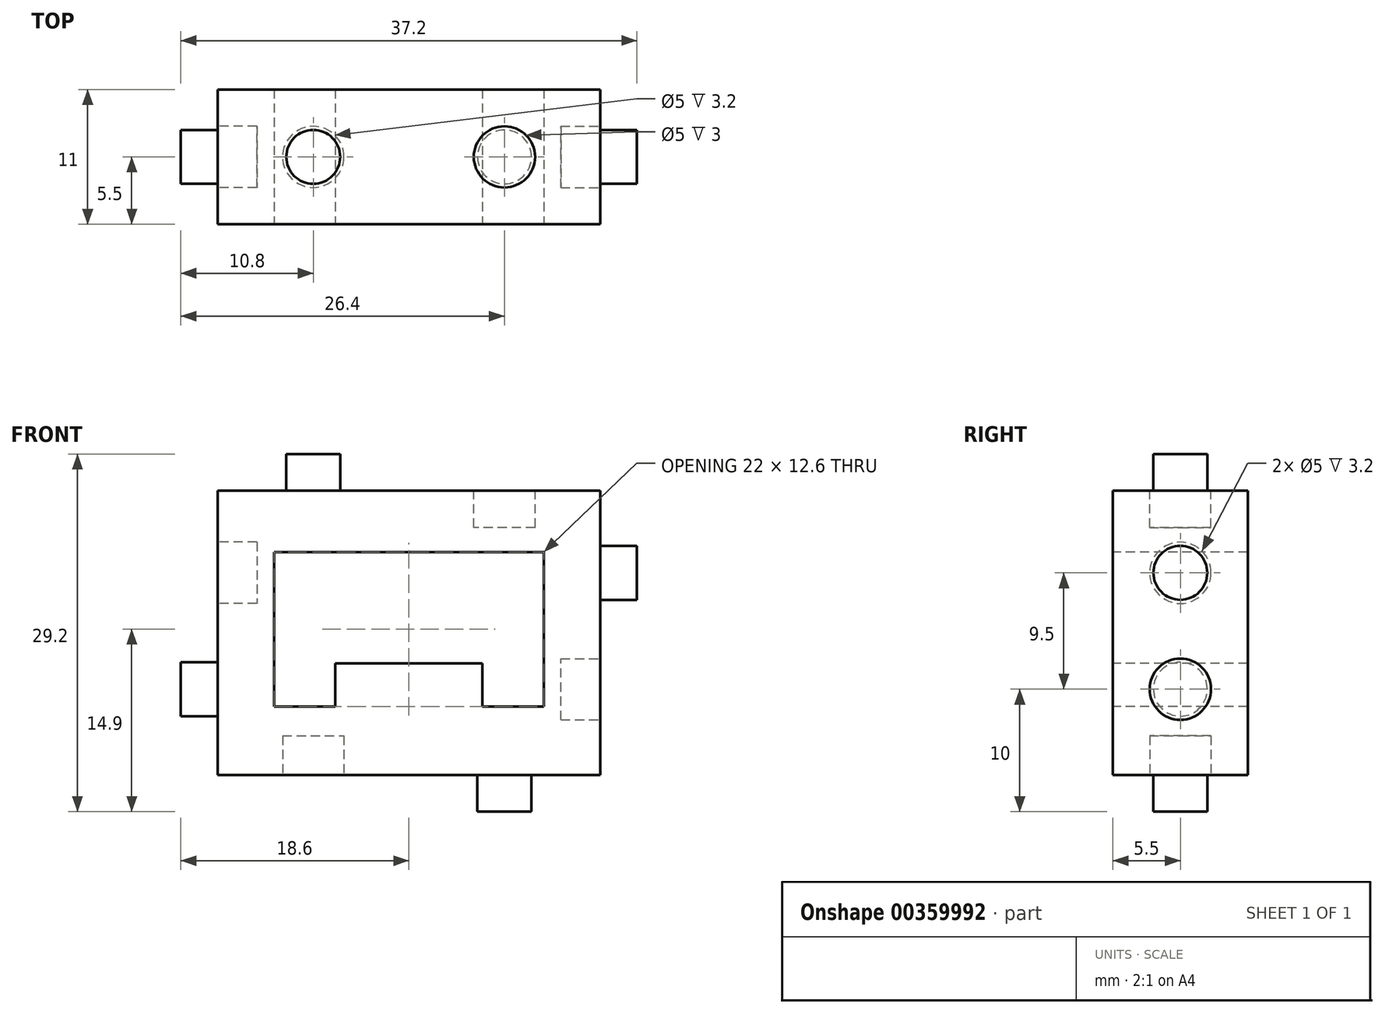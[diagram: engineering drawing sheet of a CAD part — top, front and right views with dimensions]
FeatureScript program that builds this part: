
annotation { "Feature Type Name" : "Feature", "Feature Type Description" : "" }
export const myFeature = defineFeature(function(context is Context, id is Id, definition is map)
    precondition{}
    {
        {
            var Q0;
            Q0=qCreatedBy(makeId("Top.planeOp"),FACE);
            var sketch = newSketch(context, id + "F0", { "sketchPlane" : qUnion([Q0])});
            skLineSegment(sketch, "E0.bottom", {"start": v(-15.6, 5.5) * mm, "end": v(15.6, 5.5) * mm});
            skLineSegment(sketch, "E0.top", {"start": v(-15.6, -5.5) * mm, "end": v(15.6, -5.5) * mm});
            skLineSegment(sketch, "E0.left", {"start": v(-15.6, 5.5) * mm, "end": v(-15.6, -5.5) * mm});
            skLineSegment(sketch, "E0.right", {"start": v(15.6, 5.5) * mm, "end": v(15.6, -5.5) * mm});
            skLineSegment(sketch, "E1", {"start": v(-7.8, 0) * mm, "end": v(-7.8, 14.25) * mm, "construction": true});
            skLineSegment(sketch, "E2", {"start": v(0, 13.9) * mm, "end": v(0, -15.19) * mm});
            skSolve(sketch);
        }
        {
            var Q0;
            Q0=makeQuery(id+"F0.imprint","IMPRINT",FACE,{"disambiguationData":[TD([[makeQuery(id+"F0.imprint","IMPRINT",EDGE,{"derivedFrom":sQuery(id+"F0.wireOp",EDGE,"E0.bottom")}),-1.0]])]});
            extrude(context, id + "F1", {"entities" : qUnion([Q0]), "depth" : 23.2 * mm});
        }
        {
            var Q0;
            Q0=makeQuery(id+"F1.opExtrude","SWEPT_FACE",FACE,{"disambiguationData":[OSD([sQuery(id+"F0.wireOp",EDGE,"E0.top")])]});
            var sketch = newSketch(context, id + "F2", { "sketchPlane" : qUnion([Q0])});
            skLineSegment(sketch, "E3.MirrorCS", {"start": v(-11, 18.2) * mm, "end": v(-11, 5.6) * mm});
            skLineSegment(sketch, "E4.MirrorCS", {"start": v(-6, 5.6) * mm, "end": v(-6, 9.1) * mm});
            skPoint(sketch, "E5.MirrorP", {"position": v(-11, 5.6) * mm});
            skLineSegment(sketch, "E6.MirrorCS", {"start": v(-11, 5.6) * mm, "end": v(-6, 5.6) * mm});
            skLineSegment(sketch, "E7.MirrorCS", {"start": v(0, 9.1) * mm, "end": v(-6, 9.1) * mm});
            skLineSegment(sketch, "E8.MirrorCS", {"start": v(0, 18.2) * mm, "end": v(-11, 18.2) * mm});
            skLineSegment(sketch, "E9.MirrorCS", {"start": v(0, 18.2) * mm, "end": v(11, 18.2) * mm});
            skLineSegment(sketch, "E10.MirrorCS", {"start": v(11, 18.2) * mm, "end": v(11, 5.6) * mm});
            skLineSegment(sketch, "E11.MirrorCS", {"start": v(11, 5.6) * mm, "end": v(6, 5.6) * mm});
            skLineSegment(sketch, "E12.MirrorCS", {"start": v(6, 5.6) * mm, "end": v(6, 9.1) * mm});
            skLineSegment(sketch, "E13.MirrorCS", {"start": v(0, 9.1) * mm, "end": v(6, 9.1) * mm});
            skSolve(sketch);
        }
        {
            var Q0;
            Q0=makeQuery(id+"F2.imprint","IMPRINT",FACE,{"disambiguationData":[TD([[makeQuery(id+"F2.imprint","IMPRINT",EDGE,{"derivedFrom":sQuery(id+"F2.wireOp",EDGE,"jR3wVv9S-Wn4a-DM1W-meKF-9iTBe72kzQsL.bottom")}),-1.0]])]});
            var Q1;
            Q1=makeQuery(id+"F2.imprint","IMPRINT",FACE,{"disambiguationData":[TD([[makeQuery(id+"F2.imprint","IMPRINT",EDGE,{"derivedFrom":sQuery(id+"F2.wireOp",EDGE,"E3.MirrorCS")}),1.0]])]});
            extrude(context, id + "F3", {"entities" : qUnion([Q0, Q1]), "operationType" : NewBodyOperationType.REMOVE, "oppositeDirection" : true, "depth" : 25 * mm});
        }
        {
            var Q0;
            Q0=makeQuery(id+"F1.opExtrude","CAP_FACE",FACE,{"disambiguationData":[OSD([sQuery(id+"F0.wireOp",EDGE,"E0.bottom"),sQuery(id+"F0.wireOp",EDGE,"E0.top"),sQuery(id+"F0.wireOp",EDGE,"E0.left"),sQuery(id+"F0.wireOp",EDGE,"E0.right")])],"isStart":true});
            var sketch = newSketch(context, id + "F4", { "sketchPlane" : qUnion([Q0])});
            skCircle(sketch, "E14", {"center": v(-7.8, 0) * mm, "radius": 2.5 * mm});
            skSolve(sketch);
        }
        {
            var Q0;
            Q0 = qSketchRegion(id + "F4", true);
            extrude(context, id + "F5", {"entities" : qUnion([Q0]), "operationType" : NewBodyOperationType.REMOVE, "oppositeDirection" : true, "depth" : 3.2 * mm});
        }
        {
            var Q0;
            Q0=makeQuery(id+"F1.opExtrude","CAP_FACE",FACE,{"disambiguationData":[OSD([sQuery(id+"F0.wireOp",EDGE,"E0.bottom"),sQuery(id+"F0.wireOp",EDGE,"E0.top"),sQuery(id+"F0.wireOp",EDGE,"E0.left"),sQuery(id+"F0.wireOp",EDGE,"E0.right")])],"isStart":true});
            var sketch = newSketch(context, id + "F6", { "sketchPlane" : qUnion([Q0])});
            skCircle(sketch, "E15.0", {"center": v(-7.8, 0) * mm, "radius": 2.2 * mm, "construction": true});
            skCircle(sketch, "E16.MirrorC", {"center": v(7.8, 0) * mm, "radius": 2.2 * mm});
            skSolve(sketch);
        }
        {
            var Q0;
            Q0 = qSketchRegion(id + "F6", true);
            extrude(context, id + "F7", {"entities" : qUnion([Q0]), "operationType" : NewBodyOperationType.ADD, "depth" : 3 * mm});
        }
        {
            var Q0;
            Q0=makeQuery(id+"F1.opExtrude","CAP_FACE",FACE,{"disambiguationData":[OSD([sQuery(id+"F0.wireOp",EDGE,"E0.bottom"),sQuery(id+"F0.wireOp",EDGE,"E0.top"),sQuery(id+"F0.wireOp",EDGE,"E0.left"),sQuery(id+"F0.wireOp",EDGE,"E0.right")])],"isStart":false});
            var sketch = newSketch(context, id + "F8", { "sketchPlane" : qUnion([Q0])});
            skCircle(sketch, "E17", {"center": v(-7.8, 0) * mm, "radius": 2.2 * mm});
            skSolve(sketch);
        }
        {
            var Q0;
            Q0 = qSketchRegion(id + "F8", true);
            extrude(context, id + "F9", {"entities" : qUnion([Q0]), "operationType" : NewBodyOperationType.ADD, "depth" : 3 * mm});
        }
        {
            var Q0;
            Q0=makeQuery(id+"F1.opExtrude","CAP_FACE",FACE,{"disambiguationData":[OSD([sQuery(id+"F0.wireOp",EDGE,"E0.bottom"),sQuery(id+"F0.wireOp",EDGE,"E0.top"),sQuery(id+"F0.wireOp",EDGE,"E0.left"),sQuery(id+"F0.wireOp",EDGE,"E0.right")])],"isStart":false});
            var sketch = newSketch(context, id + "F10", { "sketchPlane" : qUnion([Q0])});
            skCircle(sketch, "E18", {"center": v(7.8, 0) * mm, "radius": 2.5 * mm});
            skSolve(sketch);
        }
        {
            var Q0;
            Q0=makeQuery(id+"F10.imprint","IMPRINT",FACE,{"disambiguationData":[TD([[makeQuery(id+"F10.imprint","IMPRINT",EDGE,{"derivedFrom":sQuery(id+"F10.wireOp",EDGE,"E18")}),1.0]])]});
            var Q1;
            Q1=sQuery(id+"F10.wireOp",EDGE,"E18");
            extrude(context, id + "F11", {"entities" : qUnion([Q0]), "operationType" : NewBodyOperationType.REMOVE, "surfaceEntities" : qUnion([Q1]), "oppositeDirection" : true, "depth" : 3 * mm});
        }
        {
            var Q0;
            Q0=makeQuery(id+"F1.opExtrude","SWEPT_FACE",FACE,{"disambiguationData":[OSD([sQuery(id+"F0.wireOp",EDGE,"E0.right")])]});
            var sketch = newSketch(context, id + "F12", { "sketchPlane" : qUnion([Q0])});
            skCircle(sketch, "E19", {"center": v(0, 7) * mm, "radius": 2.5 * mm});
            skSolve(sketch);
        }
        {
            var Q0;
            Q0=makeQuery(id+"F12.imprint","IMPRINT",FACE,{"disambiguationData":[TD([[makeQuery(id+"F12.imprint","IMPRINT",EDGE,{"derivedFrom":sQuery(id+"F12.wireOp",EDGE,"E19")}),-1.0]])]});
            var sketch = newSketch(context, id + "F13", { "sketchPlane" : qUnion([Q0])});
            skCircle(sketch, "E20", {"center": v(0, 16.5) * mm, "radius": 2.2 * mm});
            skSolve(sketch);
        }
        {
            var Q0;
            Q0=makeQuery(id+"F13.imprint","IMPRINT",FACE,{"disambiguationData":[TD([[makeQuery(id+"F13.imprint","IMPRINT",EDGE,{"derivedFrom":sQuery(id+"F13.wireOp",EDGE,"E20")}),1.0]])]});
            var Q1;
            Q1=sQuery(id+"F13.wireOp",EDGE,"E20");
            extrude(context, id + "F14", {"entities" : qUnion([Q0]), "operationType" : NewBodyOperationType.ADD, "surfaceEntities" : qUnion([Q1]), "depth" : 3 * mm});
        }
        {
            var Q0;
            Q0=makeQuery(id+"F12.imprint","IMPRINT",FACE,{"disambiguationData":[TD([[makeQuery(id+"F12.imprint","IMPRINT",EDGE,{"derivedFrom":sQuery(id+"F12.wireOp",EDGE,"E19")}),1.0]])]});
            var Q1;
            Q1=sQuery(id+"F12.wireOp",EDGE,"E19");
            extrude(context, id + "F15", {"entities" : qUnion([Q0]), "operationType" : NewBodyOperationType.REMOVE, "surfaceEntities" : qUnion([Q1]), "oppositeDirection" : true, "depth" : 3.2 * mm});
        }
        {
            var Q0;
            Q0=makeQuery(id+"F1.opExtrude","SWEPT_FACE",FACE,{"disambiguationData":[OSD([sQuery(id+"F0.wireOp",EDGE,"E0.left")])]});
            var sketch = newSketch(context, id + "F16", { "sketchPlane" : qUnion([Q0])});
            skCircle(sketch, "E21", {"center": v(0, 16.5) * mm, "radius": 2.5 * mm});
            skSolve(sketch);
        }
        {
            var Q0;
            Q0=makeQuery(id+"F16.imprint","IMPRINT",FACE,{"disambiguationData":[TD([[makeQuery(id+"F16.imprint","IMPRINT",EDGE,{"derivedFrom":sQuery(id+"F16.wireOp",EDGE,"E21")}),-1.0]])]});
            var sketch = newSketch(context, id + "F17", { "sketchPlane" : qUnion([Q0])});
            skCircle(sketch, "E22", {"center": v(0, 7) * mm, "radius": 2.2 * mm});
            skSolve(sketch);
        }
        {
            var Q0;
            Q0=makeQuery(id+"F16.imprint","IMPRINT",FACE,{"disambiguationData":[TD([[makeQuery(id+"F16.imprint","IMPRINT",EDGE,{"derivedFrom":sQuery(id+"F16.wireOp",EDGE,"E21")}),1.0]])]});
            var Q1;
            Q1=sQuery(id+"F16.wireOp",EDGE,"E21");
            extrude(context, id + "F18", {"entities" : qUnion([Q0]), "operationType" : NewBodyOperationType.REMOVE, "surfaceEntities" : qUnion([Q1]), "oppositeDirection" : true, "depth" : 3.2 * mm});
        }
        {
            var Q0;
            Q0=makeQuery(id+"F17.imprint","IMPRINT",FACE,{"disambiguationData":[TD([[makeQuery(id+"F17.imprint","IMPRINT",EDGE,{"derivedFrom":sQuery(id+"F17.wireOp",EDGE,"E22")}),1.0]])]});
            var Q1;
            Q1=sQuery(id+"F17.wireOp",EDGE,"E22");
            extrude(context, id + "F19", {"entities" : qUnion([Q0]), "operationType" : NewBodyOperationType.ADD, "surfaceEntities" : qUnion([Q1]), "depth" : 3 * mm});
        }
    });
